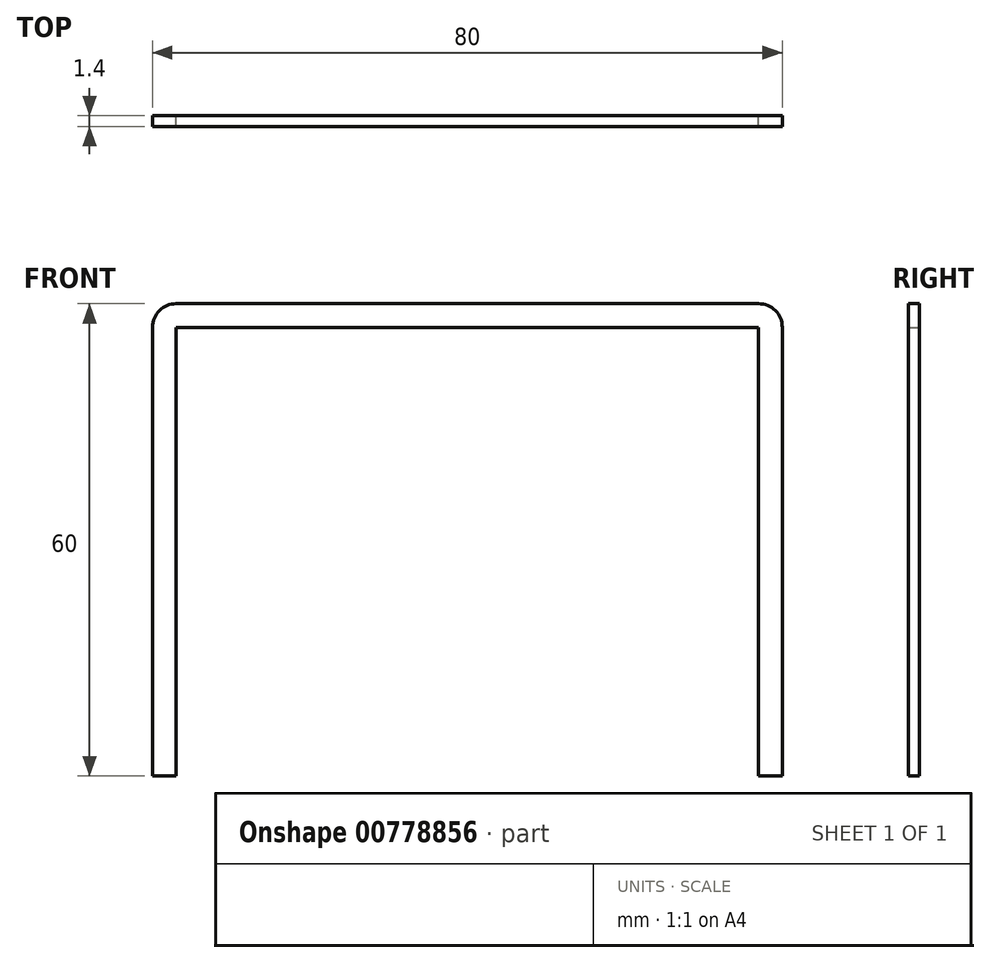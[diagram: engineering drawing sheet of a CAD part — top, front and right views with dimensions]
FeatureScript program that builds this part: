
annotation { "Feature Type Name" : "Feature", "Feature Type Description" : "" }
export const myFeature = defineFeature(function(context is Context, id is Id, definition is map)
    precondition{}
    {
        {
            var Q0;
            Q0=qCreatedBy(makeId("Front.planeOp"),FACE);
            var sketch = newSketch(context, id + "F0", { "sketchPlane" : qUnion([Q0])});
            skLineSegment(sketch, "E0.bottom", {"start": v(-37, 60) * mm, "end": v(37, 60) * mm});
            skLineSegment(sketch, "E0.top", {"start": v(-37, -60) * mm, "end": v(37, -60) * mm});
            skLineSegment(sketch, "E0.left", {"start": v(-40, 57) * mm, "end": v(-40, -57) * mm});
            skLineSegment(sketch, "E0.right", {"start": v(40, 57) * mm, "end": v(40, -57) * mm});
            skPoint(sketch, "E1.visualSharp", {"position": v(-40, 60) * mm});
            skArc(sketch, "E1.filletArc", {"start": v(-37, 60) * mm, "mid": v(-39.12, 59.12) * mm, "end": v(-40, 57) * mm});
            skPoint(sketch, "E2.visualSharp", {"position": v(40, 60) * mm});
            skArc(sketch, "E2.filletArc", {"start": v(40, 57) * mm, "mid": v(39.12, 59.12) * mm, "end": v(37, 60) * mm});
            skPoint(sketch, "E3.visualSharp", {"position": v(40, -60) * mm});
            skArc(sketch, "E3.filletArc", {"start": v(37, -60) * mm, "mid": v(39.12, -59.12) * mm, "end": v(40, -57) * mm});
            skPoint(sketch, "E4.visualSharp", {"position": v(-40, -60) * mm});
            skArc(sketch, "E4.filletArc", {"start": v(-40, -57) * mm, "mid": v(-39.12, -59.12) * mm, "end": v(-37, -60) * mm});
            skPoint(sketch, "E5", {"position": v(40, 0) * mm});
            skPoint(sketch, "E6", {"position": v(0, -60) * mm});
            skLineSegment(sketch, "E7.0", {"start": v(-37, -57) * mm, "end": v(37, -57) * mm});
            skLineSegment(sketch, "E7.1", {"start": v(-37, 57) * mm, "end": v(-37, -57) * mm});
            skLineSegment(sketch, "E7.2", {"start": v(-37, 57) * mm, "end": v(37, 57) * mm});
            skLineSegment(sketch, "E7.3", {"start": v(37, 57) * mm, "end": v(37, -57) * mm});
            skLineSegment(sketch, "E8", {"start": v(-56.76, 0) * mm, "end": v(60.43, 0) * mm});
            skSolve(sketch);
        }
        {
            var Q0;
            Q0=makeQuery(id+"F0.imprint","IMPRINT",FACE,{"disambiguationData":[TD([[makeQuery(id+"F0.imprint","IMPRINT",EDGE,{"derivedFrom":sQuery(id+"F0.wireOp",EDGE,"E0.bottom")}),-1.0]])]});
            extrude(context, id + "F1", {"entities" : qUnion([Q0]), "depth" : 1.4 * mm, "offsetDistance" : 25 * mm});
        }
    });
